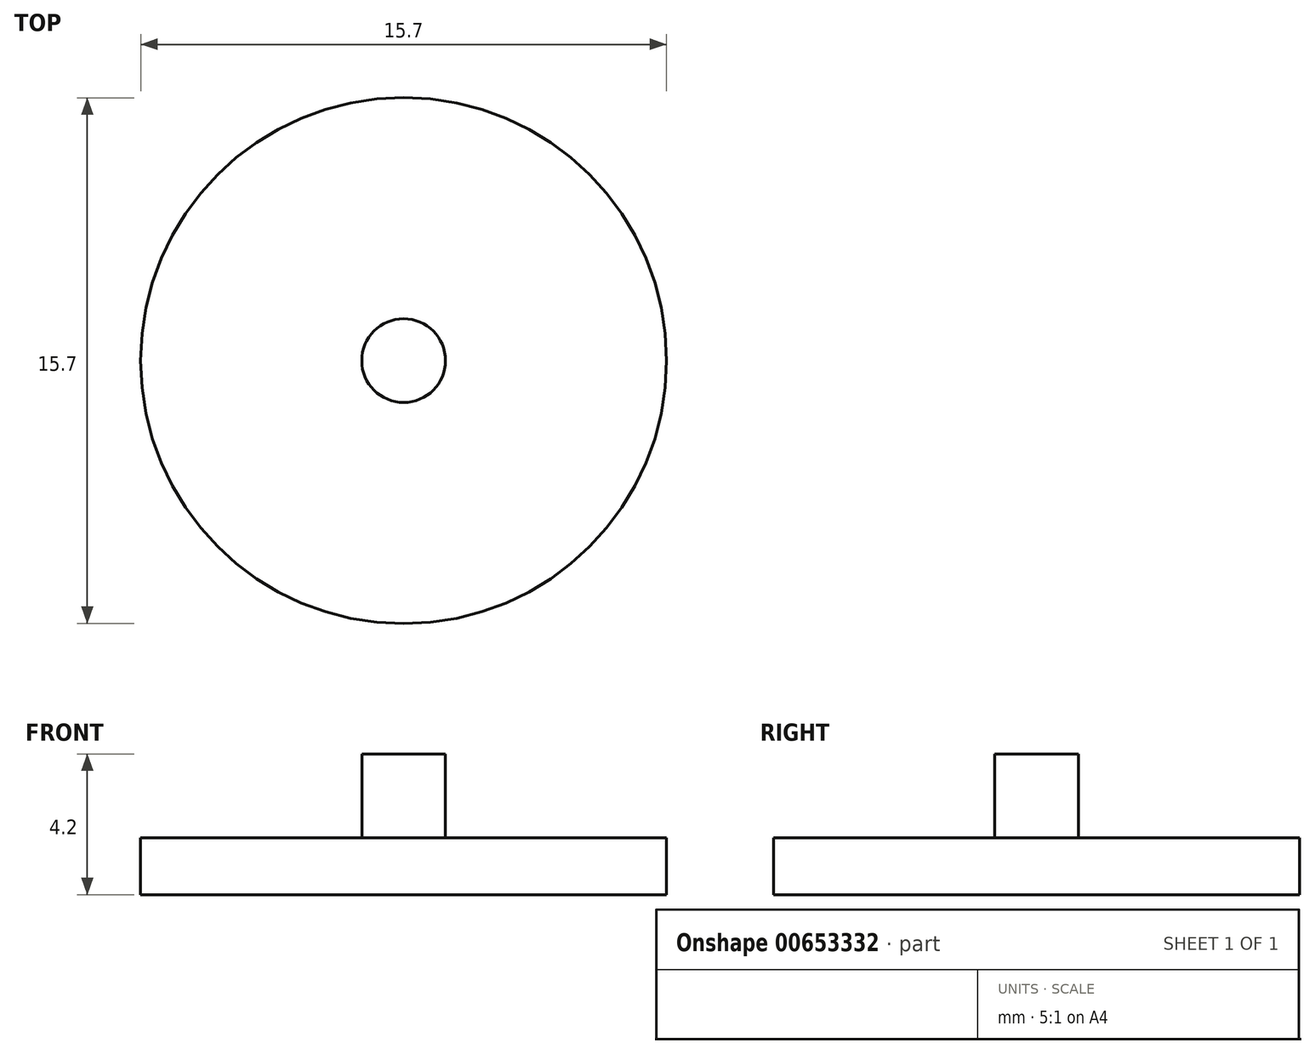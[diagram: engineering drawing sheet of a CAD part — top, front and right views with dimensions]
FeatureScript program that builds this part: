
annotation { "Feature Type Name" : "Feature", "Feature Type Description" : "" }
export const myFeature = defineFeature(function(context is Context, id is Id, definition is map)
    precondition{}
    {
        {
            var Q0;
            Q0=qCreatedBy(makeId("Top.planeOp"),FACE);
            var sketch = newSketch(context, id + "F0", { "sketchPlane" : qUnion([Q0])});
            skCircle(sketch, "E0", {"center": v(0, 0) * mm, "radius": 7.85 * mm});
            skSolve(sketch);
        }
        {
            var Q0;
            Q0=makeQuery(id+"F0.imprint","IMPRINT",FACE,{"disambiguationData":[TD([[makeQuery(id+"F0.imprint","IMPRINT",EDGE,{"derivedFrom":sQuery(id+"F0.wireOp",EDGE,"E0")}),1.0]])]});
            var sketch = newSketch(context, id + "F1", { "sketchPlane" : qUnion([Q0])});
            skCircle(sketch, "E1", {"center": v(0, 0) * mm, "radius": 1.25 * mm});
            skSolve(sketch);
        }
        {
            var Q0;
            Q0 = qSketchRegion(id + "F0", true);
            extrude(context, id + "F2", {"entities" : qUnion([Q0]), "oppositeDirection" : true, "depth" : 1.7 * mm, "offsetDistance" : 25 * mm});
        }
        {
            var Q0;
            Q0 = qSketchRegion(id + "F1", true);
            extrude(context, id + "F3", {"entities" : qUnion([Q0]), "operationType" : NewBodyOperationType.ADD, "depth" : 2.5 * mm, "offsetDistance" : 25 * mm});
        }
    });
